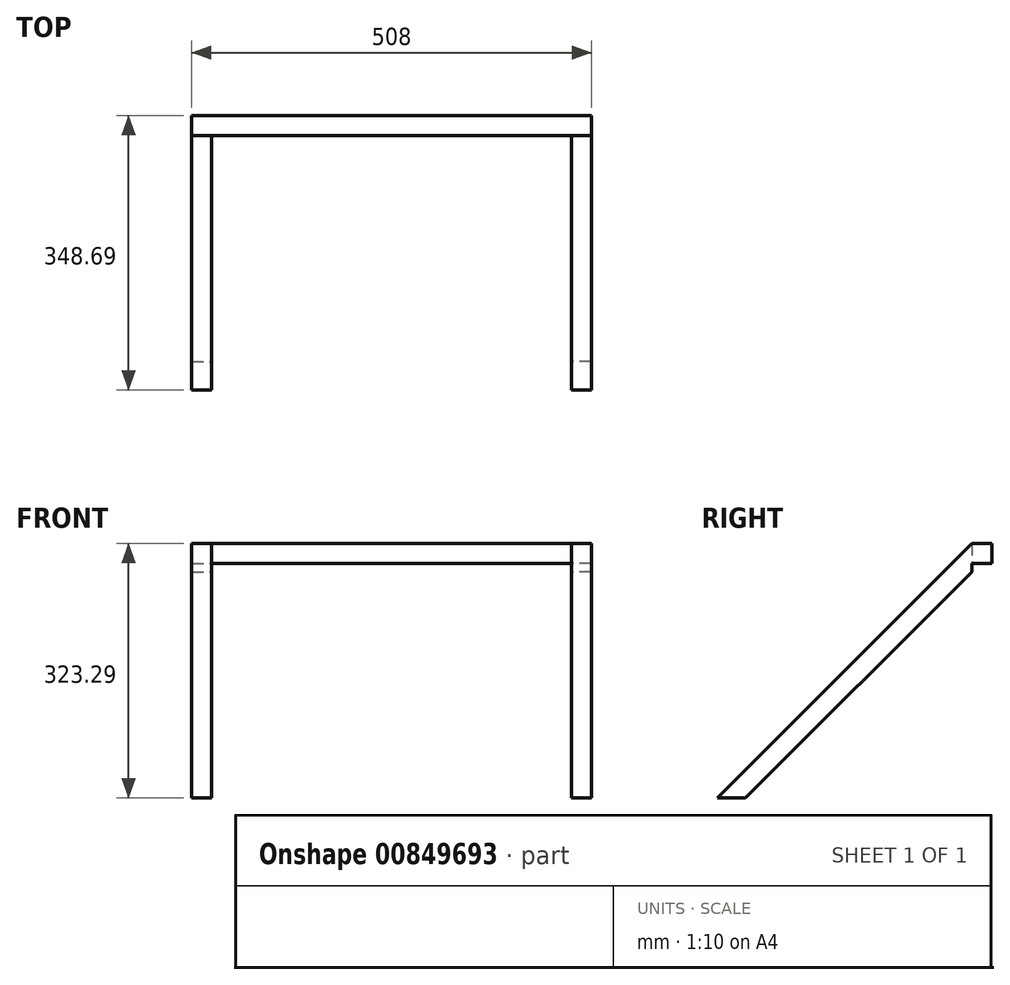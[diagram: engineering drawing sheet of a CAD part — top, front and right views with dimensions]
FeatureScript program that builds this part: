
annotation { "Feature Type Name" : "Feature", "Feature Type Description" : "" }
export const myFeature = defineFeature(function(context is Context, id is Id, definition is map)
    precondition{}
    {
        {
            var Q0;
            Q0=qCreatedBy(makeId("Right.planeOp"),FACE);
            cPlane(context, id + "F0", {"entities" : qUnion([Q0]), "cplaneType" : CPlaneType.OFFSET, "offset" : 228.6 * mm, "width" : 152.4 * mm, "height" : 152.4 * mm});
        }
        {
            var Q0;
            Q0=qCreatedBy(id+"F0.planeOp",FACE);
            var sketch = newSketch(context, id + "F1", { "sketchPlane" : qUnion([Q0])});
            skLineSegment(sketch, "E0", {"start": v(0, 0) * mm, "end": v(323.29, 323.29) * mm});
            skLineSegment(sketch, "E1", {"start": v(323.29, 287.37) * mm, "end": v(35.92, 0) * mm});
            skLineSegment(sketch, "E2", {"start": v(35.92, 0) * mm, "end": v(0, 0) * mm});
            skLineSegment(sketch, "E3", {"start": v(323.29, 323.29) * mm, "end": v(323.29, 287.37) * mm});
            skSolve(sketch);
        }
        {
            var Q0;
            Q0=makeQuery(id+"F1.imprint","IMPRINT",FACE,{"disambiguationData":[TD([[makeQuery(id+"F1.imprint","IMPRINT",EDGE,{"derivedFrom":sQuery(id+"F1.wireOp",EDGE,"E0")}),-1.0]])]});
            extrude(context, id + "F2", {"entities" : qUnion([Q0]), "depth" : 25.4 * mm, "offsetDistance" : 25.4 * mm});
        }
        {
            var Q0;
            Q0=qCreatedBy(makeId("Right.planeOp"),FACE);
            var sketch = newSketch(context, id + "F3", { "sketchPlane" : qUnion([Q0])});
            skLineSegment(sketch, "E4.bottom", {"start": v(348.69, 323.29) * mm, "end": v(323.29, 323.29) * mm});
            skLineSegment(sketch, "E4.top", {"start": v(348.69, 297.89) * mm, "end": v(323.29, 297.89) * mm});
            skLineSegment(sketch, "E4.left", {"start": v(348.69, 323.29) * mm, "end": v(348.69, 297.89) * mm});
            skLineSegment(sketch, "E4.right", {"start": v(323.29, 323.29) * mm, "end": v(323.29, 297.89) * mm});
            skSolve(sketch);
        }
        {
            var Q0;
            Q0=makeQuery(id+"F3.imprint","IMPRINT",FACE,{"disambiguationData":[TD([[makeQuery(id+"F3.imprint","IMPRINT",EDGE,{"derivedFrom":sQuery(id+"F3.wireOp",EDGE,"E4.bottom")}),1.0]])]});
            var Q1;
            Q1=makeQuery(id+"F2.opExtrude","CAP_FACE",FACE,{"disambiguationData":[OSD([sQuery(id+"F1.wireOp",EDGE,"E0"),sQuery(id+"F1.wireOp",EDGE,"E1"),sQuery(id+"F1.wireOp",EDGE,"E2"),sQuery(id+"F1.wireOp",EDGE,"E3")])],"isStart":false});
            extrude(context, id + "F4", {"entities" : qUnion([Q0]), "operationType" : NewBodyOperationType.ADD, "endBound" : BoundingType.UP_TO_SURFACE, "depth" : 25.4 * mm, "endBoundEntityFace" : qUnion([Q1]), "offsetDistance" : 25.4 * mm});
        }
        {
            var Q0;
            Q0=makeQuery(id+"F2.opExtrude","SWEPT_BODY",BODY,{"disambiguationData":[OSD([sQuery(id+"F1.wireOp",EDGE,"E0"),sQuery(id+"F1.wireOp",EDGE,"E1"),sQuery(id+"F1.wireOp",EDGE,"E2"),sQuery(id+"F1.wireOp",EDGE,"E3")])]});
            var Q1;
            Q1=qCreatedBy(makeId("Right.planeOp"),FACE);
            mirror(context, id + "F5", {"operationType" : NewBodyOperationType.ADD, "entities" : qUnion([Q0]), "mirrorPlane" : qUnion([Q1])});
        }
    });
